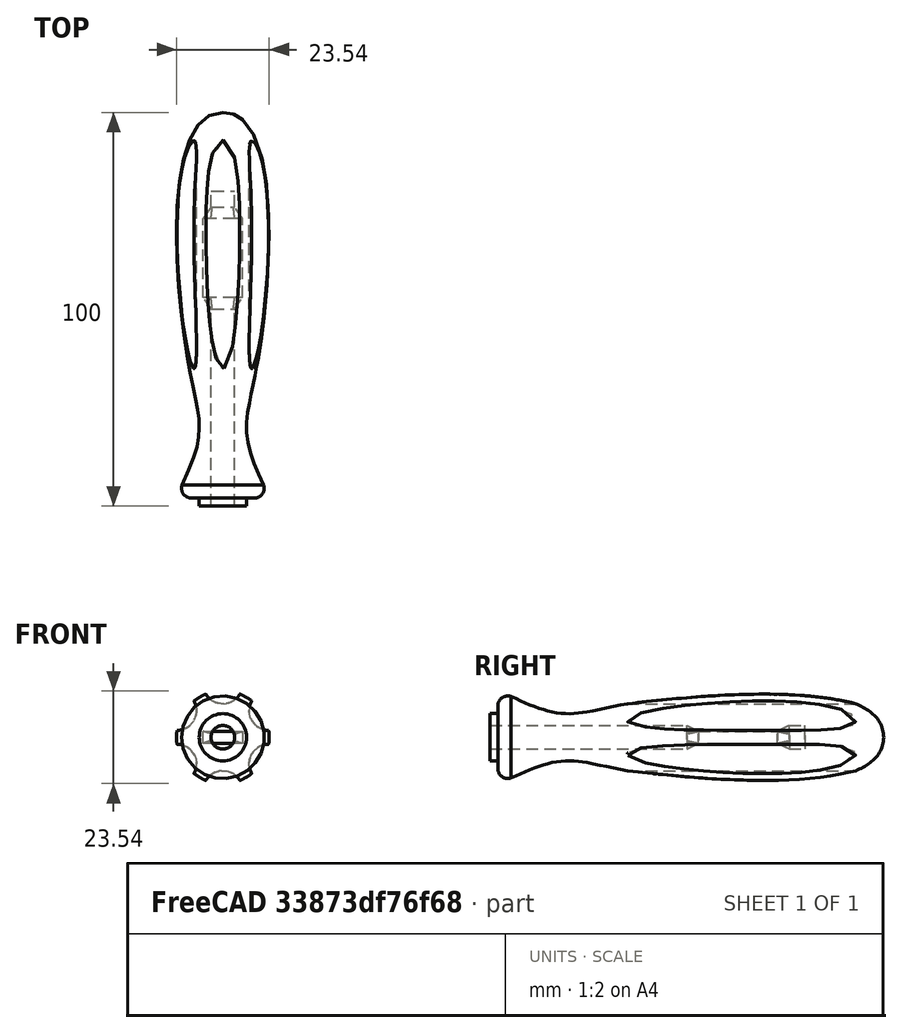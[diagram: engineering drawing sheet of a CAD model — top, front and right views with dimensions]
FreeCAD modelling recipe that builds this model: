
FCSTD DOCUMENT  (FreeCAD 0.17R13247 (Git))
Label: CHAVE FENDA-CJ
License: All rights reserved
LicenseURL: http://en.wikipedia.org/wiki/All_rights_reserved
objects: Part::FeaturePython×2, App::FeaturePython×2, Part::Cut×1
note: 3 computed .brp shape members not serialized (recipe doc carries the construction recipe); baked Part::Feature solids carry a one-line shape summary decoded from their .brp

FEATURE [Part::FeaturePython] CHAVE_FENDA_1_01  # a2plus imported part (geometry in sourceFile) (typed FeaturePython)
  Placement = pos=(0,0,0) rot=(1,0,0;1.5708rad)
  fixedPosition = true
  sourceFile = <path> DE FENDA/CHAVE FENDA-1.FCStd
  timeLastImport = 1.52339e+09
  updateColors = true
FEATURE [Part::FeaturePython] CHAVE_FENDA_2_01  # a2plus imported part (geometry in sourceFile) (typed FeaturePython)
  Placement = pos=(0,100,0) rot=(0,0,1;0rad)
  fixedPosition = false
  sourceFile = <path> DE FENDA/CHAVE FENDA-2.FCStd
  timeLastImport = 1.52339e+09
  updateColors = true
FEATURE [App::FeaturePython] circularEdgeConstraint01  label="circularEdgeConstraint01__CHAVE_FENDA_2_01"  # a2plus constraint (typed FeaturePython)
  Object1 = CHAVE_FENDA_1_01
  Object2 = CHAVE_FENDA_2_01
  SubElement1 = Edge176
  SubElement2 = Edge1
  Type = circularEdge
  directionConstraint = 1
  lockRotation = false
  offset = -80
FEATURE [App::FeaturePython] circularEdgeConstraint01_mirror  label="circularEdgeConstraint01__CHAVE_FENDA_1_01"  # a2plus constraint (typed FeaturePython)
  Object1 = CHAVE_FENDA_1_01
  Object2 = CHAVE_FENDA_2_01
  SubElement1 = Edge176
  SubElement2 = Edge1
  Type = circularEdge
  directionConstraint = 1
  lockRotation = false
  offset = -80
FEATURE [Part::Cut] Cut
  Base = -> CHAVE_FENDA_2_01
  Tool = -> CHAVE_FENDA_1_01
note: 2 file-system paths scrubbed to <path> (originals preserved in the JSON sidecar)
